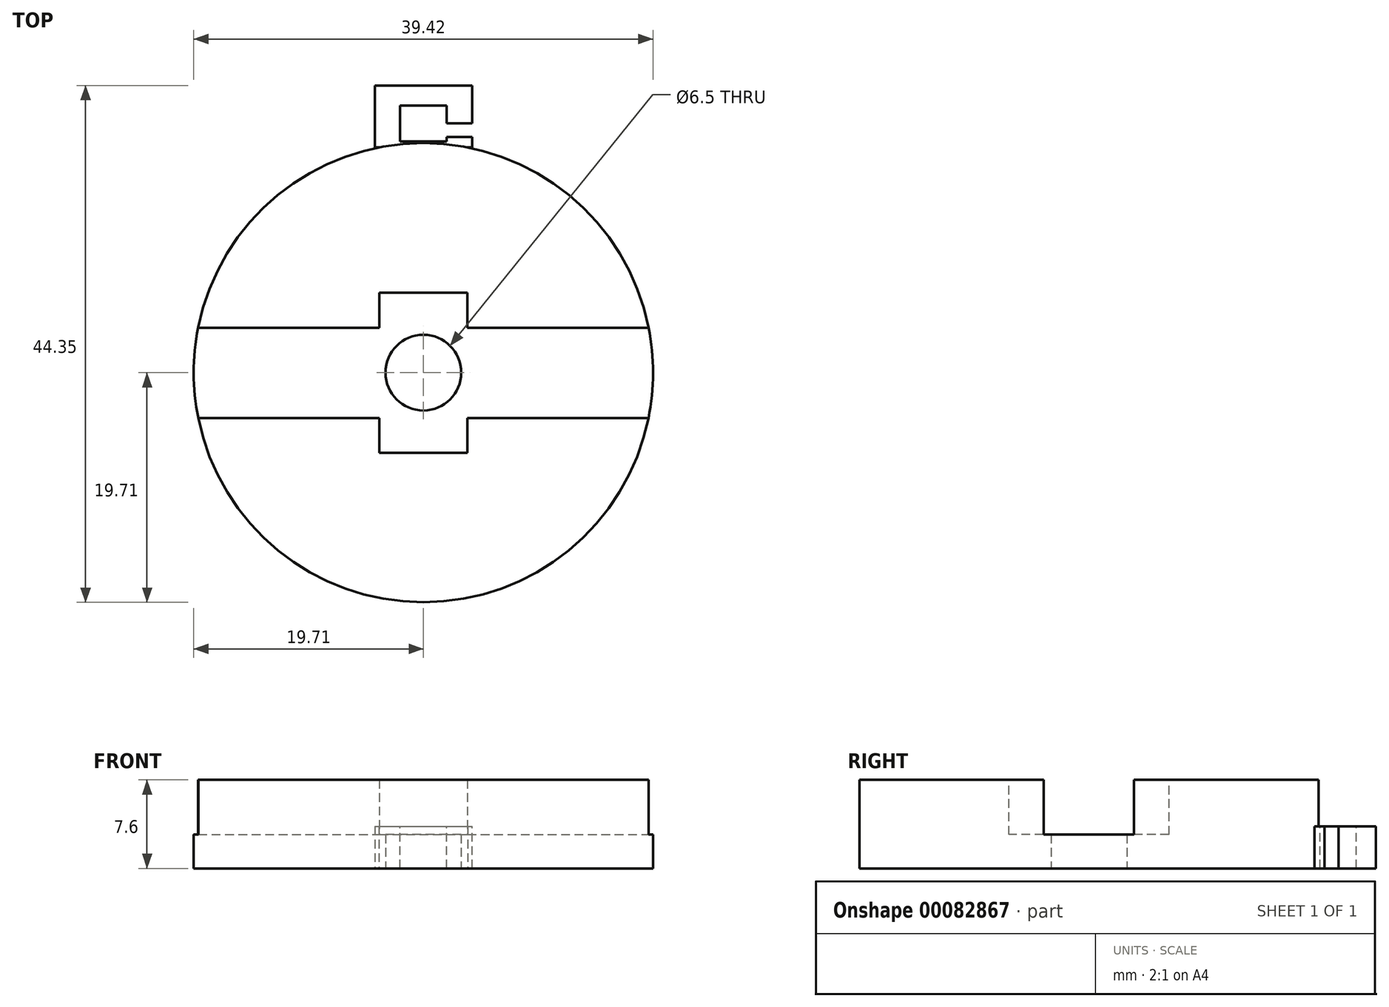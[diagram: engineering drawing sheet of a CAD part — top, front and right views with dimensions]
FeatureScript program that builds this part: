
annotation { "Feature Type Name" : "Feature", "Feature Type Description" : "" }
export const myFeature = defineFeature(function(context is Context, id is Id, definition is map)
    precondition{}
    {
        {
            var Q0;
            Q0=qCreatedBy(makeId("Top.planeOp"),FACE);
            var sketch = newSketch(context, id + "F0", { "sketchPlane" : qUnion([Q0])});
            skCircle(sketch, "E0", {"center": v(0, 0) * mm, "radius": 19.71 * mm});
            skSolve(sketch);
        }
        {
            var Q0;
            Q0=qSketchRegion(id+"F0",true);
            extrude(context, id + "F1", {"entities" : qUnion([Q0]), "depth" : 7.6 * mm});
        }
        {
            var Q0;
            Q0=makeQuery(id+"F1.opExtrude","CAP_FACE",FACE,{"disambiguationData":[OSD([sQuery(id+"F0.wireOp",EDGE,"E0")])],"isStart":false});
            var sketch = newSketch(context, id + "F2", { "sketchPlane" : qUnion([Q0])});
            skLineSegment(sketch, "E1.bottom", {"start": v(-20, 3.85) * mm, "end": v(20, 3.85) * mm});
            skLineSegment(sketch, "E1.top", {"start": v(-20, -3.9) * mm, "end": v(20, -3.9) * mm});
            skLineSegment(sketch, "E1.left", {"start": v(-20, 3.85) * mm, "end": v(-20, -3.9) * mm});
            skLineSegment(sketch, "E1.right", {"start": v(20, 3.85) * mm, "end": v(20, -3.9) * mm});
            skSolve(sketch);
        }
        {
            var Q0;
            Q0=qSketchRegion(id+"F2",true);
            extrude(context, id + "F3", {"entities" : qUnion([Q0]), "operationType" : NewBodyOperationType.REMOVE, "oppositeDirection" : true, "depth" : 4.7 * mm});
        }
        {
            var Q0;
            {var subQ0=sQuery(id+"F0.wireOp",EDGE,"E0");Q0=makeQuery(id+"F3.boolean.opBoolean","SPLIT",FACE,{"disambiguationData":[TD([makeQuery(id+"F3.opExtrude","SWEPT_FACE",FACE,{"disambiguationData":[OSD([sQuery(id+"F2.wireOp",EDGE,"E1.bottom")])]})])],"derivedFrom":makeQuery(id+"F1.opExtrude","CAP_FACE",FACE,{"disambiguationData":[OSD([subQ0])],"isStart":false})});}
            var sketch = newSketch(context, id + "F4", { "sketchPlane" : qUnion([Q0])});
            skLineSegment(sketch, "E2.bottom", {"start": v(-3.78, 6.88) * mm, "end": v(3.78, 6.88) * mm});
            skLineSegment(sketch, "E2.top", {"start": v(-3.78, -6.88) * mm, "end": v(3.78, -6.88) * mm});
            skLineSegment(sketch, "E2.left", {"start": v(-3.78, 6.88) * mm, "end": v(-3.78, -6.88) * mm});
            skLineSegment(sketch, "E2.right", {"start": v(3.77, 6.88) * mm, "end": v(3.78, -6.88) * mm});
            skSolve(sketch);
        }
        {
            var Q0;
            Q0=qSketchRegion(id+"F4",true);
            extrude(context, id + "F5", {"entities" : qUnion([Q0]), "operationType" : NewBodyOperationType.REMOVE, "oppositeDirection" : true, "depth" : 4.7 * mm});
        }
        {
            var Q0;
            Q0=makeQuery(id+"F1.opExtrude","CAP_FACE",FACE,{"disambiguationData":[OSD([sQuery(id+"F0.wireOp",EDGE,"E0")])],"isStart":true});
            var sketch = newSketch(context, id + "F6", { "sketchPlane" : qUnion([Q0])});
            skLineSegment(sketch, "E3.bottom", {"start": v(-4.18, -19.34) * mm, "end": v(4.17, -19.34) * mm});
            skLineSegment(sketch, "E3.top", {"start": v(-4.18, -24.64) * mm, "end": v(4.18, -24.64) * mm});
            skLineSegment(sketch, "E3.left", {"start": v(-4.18, -19.34) * mm, "end": v(-4.18, -24.64) * mm});
            skLineSegment(sketch, "E3.right", {"start": v(4.17, -19.34) * mm, "end": v(4.17, -24.64) * mm});
            skSolve(sketch);
        }
        {
            var Q0;
            Q0=qSketchRegion(id+"F6",true);
            extrude(context, id + "F7", {"entities" : qUnion([Q0]), "operationType" : NewBodyOperationType.ADD, "oppositeDirection" : true, "depth" : 3.6 * mm});
        }
        {
            var Q0;
            Q0=makeQuery(id+"F7.opExtrude","CAP_FACE",FACE,{"disambiguationData":[OSD([sQuery(id+"F6.wireOp",EDGE,"E3.bottom"),sQuery(id+"F6.wireOp",EDGE,"E3.top"),sQuery(id+"F6.wireOp",EDGE,"E3.left"),sQuery(id+"F6.wireOp",EDGE,"E3.right")])],"isStart":false});
            var sketch = newSketch(context, id + "F8", { "sketchPlane" : qUnion([Q0])});
            skLineSegment(sketch, "E4.bottom", {"start": v(-2, 22.94) * mm, "end": v(2, 22.94) * mm});
            skLineSegment(sketch, "E4.top", {"start": v(-2, 19.84) * mm, "end": v(2, 19.84) * mm});
            skLineSegment(sketch, "E4.left", {"start": v(-2, 22.94) * mm, "end": v(-2, 19.84) * mm});
            skLineSegment(sketch, "E4.right", {"start": v(2, 22.94) * mm, "end": v(2, 19.84) * mm});
            skLineSegment(sketch, "E5.bottom", {"start": v(2, 21.42) * mm, "end": v(4.17, 21.42) * mm});
            skLineSegment(sketch, "E5.top", {"start": v(2, 20.22) * mm, "end": v(4.17, 20.22) * mm});
            skLineSegment(sketch, "E5.left", {"start": v(2, 21.42) * mm, "end": v(2, 20.22) * mm});
            skLineSegment(sketch, "E5.right", {"start": v(4.17, 21.42) * mm, "end": v(4.17, 20.22) * mm});
            skSolve(sketch);
        }
        {
            var Q0;
            Q0=qSketchRegion(id+"F8",true);
            extrude(context, id + "F9", {"entities" : qUnion([Q0]), "operationType" : NewBodyOperationType.REMOVE, "endBound" : BoundingType.THROUGH_ALL, "oppositeDirection" : true, "depth" : 25 * mm});
        }
        {
            var Q0;
            Q0=makeQuery(id+"F7.boolean.opBoolean","MERGE",FACE,{"derivedFrom":[makeQuery(id+"F1.opExtrude","CAP_FACE",FACE,{"disambiguationData":[OSD([sQuery(id+"F0.wireOp",EDGE,"E0")])],"isStart":true}),makeQuery(id+"F7.opExtrude","CAP_FACE",FACE,{"disambiguationData":[OSD([sQuery(id+"F6.wireOp",EDGE,"E3.bottom"),sQuery(id+"F6.wireOp",EDGE,"E3.top"),sQuery(id+"F6.wireOp",EDGE,"E3.left"),sQuery(id+"F6.wireOp",EDGE,"E3.right")])],"isStart":true})]});
            var sketch = newSketch(context, id + "F10", { "sketchPlane" : qUnion([Q0])});
            skCircle(sketch, "E6", {"center": v(0, 0) * mm, "radius": 3.25 * mm});
            skSolve(sketch);
        }
        {
            var Q0;
            Q0=qSketchRegion(id+"F10",true);
            extrude(context, id + "F11", {"entities" : qUnion([Q0]), "operationType" : NewBodyOperationType.REMOVE, "oppositeDirection" : true, "depth" : 3 * mm});
        }
    });
